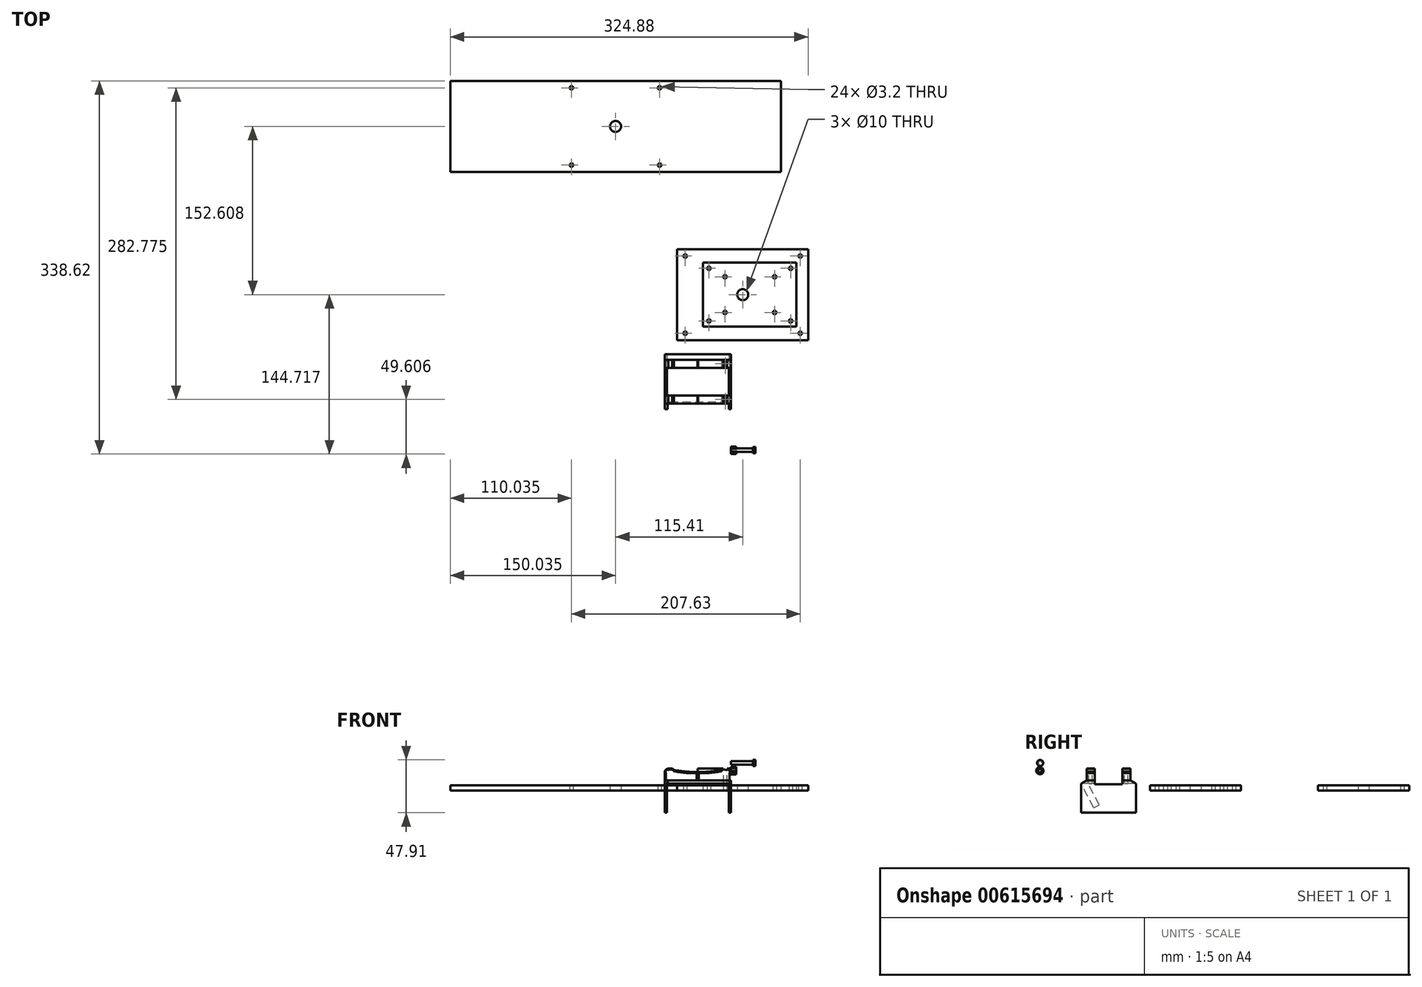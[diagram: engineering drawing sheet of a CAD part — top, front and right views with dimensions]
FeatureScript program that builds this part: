
annotation { "Feature Type Name" : "Feature", "Feature Type Description" : "" }
export const myFeature = defineFeature(function(context is Context, id is Id, definition is map)
    precondition{}
    {
        {
            var Q0;
            Q0=qCreatedBy(makeId("Right.planeOp"),FACE);
            var sketch = newSketch(context, id + "F0", { "sketchPlane" : qUnion([Q0])});
            skLineSegment(sketch, "E0.bottom", {"start": v(-19.87, 20) * mm, "end": v(-12.5, 20) * mm});
            skLineSegment(sketch, "E0.top", {"start": v(-25, -20) * mm, "end": v(25, -20) * mm});
            skLineSegment(sketch, "E0.left", {"start": v(-25, 6.62) * mm, "end": v(-25, -20) * mm});
            skLineSegment(sketch, "E0.right", {"start": v(25, 6.62) * mm, "end": v(25, -20) * mm});
            skPoint(sketch, "E0.middle", {"position": v(0, 0) * mm});
            skLineSegment(sketch, "E1", {"start": v(-12.5, 20) * mm, "end": v(-12.5, 5.9) * mm});
            skLineSegment(sketch, "E2", {"start": v(-12.5, 5.9) * mm, "end": v(0, 5.9) * mm});
            skLineSegment(sketch, "E3", {"start": v(-19.87, 20) * mm, "end": v(-19.87, 9.27) * mm});
            skLineSegment(sketch, "E4", {"start": v(-19.87, 9.27) * mm, "end": v(-25, 6.62) * mm});
            skPoint(sketch, "E5.orphan", {"position": v(-25, 20) * mm});
            skLineSegment(sketch, "E6.MirrorCS", {"start": v(12.5, 20) * mm, "end": v(12.5, 5.9) * mm});
            skLineSegment(sketch, "E7.MirrorCS", {"start": v(12.5, 5.9) * mm, "end": v(0, 5.9) * mm});
            skLineSegment(sketch, "E8.MirrorCS", {"start": v(19.87, 20) * mm, "end": v(19.87, 9.27) * mm});
            skLineSegment(sketch, "E9.MirrorCS", {"start": v(19.87, 9.27) * mm, "end": v(25, 6.62) * mm});
            skLineSegment(sketch, "E10.trimOffspring", {"start": v(12.5, 20) * mm, "end": v(19.87, 20) * mm});
            skPoint(sketch, "E11.orphan", {"position": v(25, 20) * mm});
            skCircle(sketch, "E12", {"center": v(-62.07, 25.12) * mm, "radius": 1.6 * mm});
            skCircle(sketch, "E13", {"center": v(-62.32, 18.1) * mm, "radius": 1.6 * mm});
            skCircle(sketch, "E14.cCircle", {"center": v(-62.32, 18.1) * mm, "radius": 3.2 * mm, "construction": true});
            skLineSegment(sketch, "E14.0", {"start": v(-65.79, 17.93) * mm, "end": v(-64.89, 20.43) * mm});
            skLineSegment(sketch, "E14.1", {"start": v(-64.89, 20.43) * mm, "end": v(-62.48, 21.56) * mm});
            skLineSegment(sketch, "E14.2", {"start": v(-62.48, 21.56) * mm, "end": v(-59.98, 20.66) * mm});
            skLineSegment(sketch, "E14.3", {"start": v(-59.98, 20.66) * mm, "end": v(-58.85, 18.26) * mm});
            skLineSegment(sketch, "E14.4", {"start": v(-58.85, 18.26) * mm, "end": v(-59.75, 15.75) * mm});
            skLineSegment(sketch, "E14.5", {"start": v(-59.75, 15.75) * mm, "end": v(-62.15, 14.62) * mm});
            skLineSegment(sketch, "E14.6", {"start": v(-62.15, 14.62) * mm, "end": v(-64.65, 15.52) * mm});
            skLineSegment(sketch, "E14.7", {"start": v(-64.65, 15.52) * mm, "end": v(-65.79, 17.93) * mm});
            skPoint(sketch, "E14.0.midPoint", {"position": v(-65.34, 19.18) * mm});
            skLineSegment(sketch, "E15.MirrorCS", {"start": v(-62.48, -21.56) * mm, "end": v(-59.98, -20.66) * mm});
            skLineSegment(sketch, "E16.MirrorCS", {"start": v(-64.89, -20.43) * mm, "end": v(-62.48, -21.56) * mm});
            skLineSegment(sketch, "E17.MirrorCS", {"start": v(-64.65, -15.52) * mm, "end": v(-65.79, -17.93) * mm});
            skLineSegment(sketch, "E18.MirrorCS", {"start": v(-58.85, -18.26) * mm, "end": v(-59.75, -15.75) * mm});
            skLineSegment(sketch, "E19.MirrorCS", {"start": v(-65.79, -17.93) * mm, "end": v(-64.89, -20.43) * mm});
            skLineSegment(sketch, "E20.MirrorCS", {"start": v(-62.15, -14.62) * mm, "end": v(-64.65, -15.52) * mm});
            skLineSegment(sketch, "E21.MirrorCS", {"start": v(-59.75, -15.75) * mm, "end": v(-62.15, -14.62) * mm});
            skCircle(sketch, "E22.MirrorC", {"center": v(-62.32, -18.1) * mm, "radius": 1.6 * mm});
            skLineSegment(sketch, "E23.MirrorCS", {"start": v(-59.98, -20.66) * mm, "end": v(-58.85, -18.26) * mm});
            skCircle(sketch, "E24.MirrorC", {"center": v(-62.32, -18.1) * mm, "radius": 3.2 * mm, "construction": true});
            skPoint(sketch, "E25.MirrorP", {"position": v(-65.34, -19.18) * mm});
            skSolve(sketch);
        }
        {
            var Q0;
            Q0=makeQuery(id+"F0.imprint","IMPRINT",FACE,{"disambiguationData":[TD([[makeQuery(id+"F0.imprint","IMPRINT",EDGE,{"derivedFrom":sQuery(id+"F0.wireOp",EDGE,"E0.bottom")}),-1.0]])]});
            extrude(context, id + "F1", {"entities" : qUnion([Q0]), "oppositeDirection" : true, "depth" : 60 * mm, "offsetDistance" : 25 * mm});
        }
        {
            var Q0;
            Q0=makeQuery(id+"F1.opExtrude","SWEPT_FACE",FACE,{"disambiguationData":[OSD([sQuery(id+"F0.wireOp",EDGE,"E3")])]});
            var sketch = newSketch(context, id + "F2", { "sketchPlane" : qUnion([Q0])});
            skArc(sketch, "E26", {"start": v(-56.45, 20) * mm, "mid": v(-59.1, 18.91) * mm, "end": v(-60, 16.18) * mm});
            skLineSegment(sketch, "E27", {"start": v(-30, 20) * mm, "end": v(-30, 9.27) * mm});
            skArc(sketch, "E28.MirrorCS", {"start": v(-3.55, 20) * mm, "mid": v(-0.9, 18.91) * mm, "end": v(0, 16.18) * mm});
            skArc(sketch, "E29", {"start": v(-51.52, 18.72) * mm, "mid": v(-52.28, 19.52) * mm, "end": v(-53.28, 20) * mm});
            skArc(sketch, "E30.MirrorCS", {"start": v(-8.48, 18.72) * mm, "mid": v(-7.72, 19.52) * mm, "end": v(-6.72, 20) * mm});
            skArc(sketch, "E31", {"start": v(-51.52, 18.72) * mm, "mid": v(-30, 16.9) * mm, "end": v(-8.48, 18.72) * mm});
            skPoint(sketch, "E32.orphan", {"position": v(-51.06, 16.58) * mm});
            skPoint(sketch, "E33.orphan", {"position": v(-8.94, 16.58) * mm});
            skLineSegment(sketch, "E34", {"start": v(-58.92, 9.27) * mm, "end": v(-58.92, 15.97) * mm});
            skLineSegment(sketch, "E35", {"start": v(-30.9, 15.88) * mm, "end": v(-30.9, 9.27) * mm});
            skArc(sketch, "E36", {"start": v(-51.92, 17.72) * mm, "mid": v(-41.46, 16.24) * mm, "end": v(-30.9, 15.88) * mm});
            skArc(sketch, "E37", {"start": v(-56.43, 18.92) * mm, "mid": v(-58.7, 18.3) * mm, "end": v(-58.92, 15.97) * mm});
            skArc(sketch, "E38", {"start": v(-51.92, 17.72) * mm, "mid": v(-52.22, 18.8) * mm, "end": v(-53.3, 19.1) * mm});
            skLineSegment(sketch, "E39", {"start": v(-56.43, 18.92) * mm, "end": v(-53.3, 19.1) * mm});
            skArc(sketch, "E40.MirrorCS", {"start": v(-8.08, 17.72) * mm, "mid": v(-18.54, 16.24) * mm, "end": v(-29.1, 15.88) * mm});
            skArc(sketch, "E41.MirrorCS", {"start": v(-8.08, 17.72) * mm, "mid": v(-7.78, 18.8) * mm, "end": v(-6.7, 19.1) * mm});
            skLineSegment(sketch, "E42.MirrorCS", {"start": v(-3.57, 18.92) * mm, "end": v(-6.7, 19.1) * mm});
            skArc(sketch, "E43.MirrorCS", {"start": v(-3.57, 18.92) * mm, "mid": v(-1.3, 18.3) * mm, "end": v(-1.08, 15.97) * mm});
            skLineSegment(sketch, "E44.MirrorCS", {"start": v(-1.08, 9.27) * mm, "end": v(-1.08, 15.97) * mm});
            skLineSegment(sketch, "E45.MirrorCS", {"start": v(-29.1, 15.88) * mm, "end": v(-29.1, 9.27) * mm});
            skSolve(sketch);
        }
        {
            var Q0;
            {var subQ0=sQuery(id+"F2.wireOp",EDGE,"E26");var subQ1=sQuery(id+"F0.wireOp",EDGE,"E3");var subQ4=makeQuery(id+"F1.opExtrude","CAP_EDGE",EDGE,{"disambiguationData":[OSD([subQ1])],"isStart":false});var subQ5=makeQuery(id+"F2.imprint","INTERSECT",VERTEX,{"disambiguationData":[OD(1.0)],"derivedFrom":[subQ4,subQ0]});Q0=makeQuery(id+"F2.imprint","IMPRINT",FACE,{"disambiguationData":[TD([[makeQuery(id+"F2.imprint","IMPRINT",EDGE,{"disambiguationData":[TD([[subQ5,1.0]])],"derivedFrom":subQ0}),-1.0]])]});}
            var Q1;
            {var subQ0=sQuery(id+"F2.wireOp",EDGE,"E28.MirrorCS");var subQ1=sQuery(id+"F0.wireOp",EDGE,"E3");var subQ4=makeQuery(id+"F1.opExtrude","CAP_EDGE",EDGE,{"disambiguationData":[OSD([subQ1])],"isStart":true});var subQ5=makeQuery(id+"F2.imprint","INTERSECT",VERTEX,{"disambiguationData":[OD(1.0)],"derivedFrom":[subQ4,subQ0]});Q1=makeQuery(id+"F2.imprint","IMPRINT",FACE,{"disambiguationData":[TD([[makeQuery(id+"F2.imprint","IMPRINT",EDGE,{"disambiguationData":[TD([[subQ5,1.0]])],"derivedFrom":subQ0}),1.0]])]});}
            var Q2;
            {var subQ5=sQuery(id+"F2.wireOp",EDGE,"E29");Q2=makeQuery(id+"F2.imprint","IMPRINT",FACE,{"disambiguationData":[TD([[makeQuery(id+"F2.imprint","IMPRINT",EDGE,{"derivedFrom":subQ5}),-1.0]])]});}
            var Q3;
            {var subQ5=sQuery(id+"F2.wireOp",EDGE,"E30.MirrorCS");Q3=makeQuery(id+"F2.imprint","IMPRINT",FACE,{"disambiguationData":[TD([[makeQuery(id+"F2.imprint","IMPRINT",EDGE,{"derivedFrom":subQ5}),1.0]])]});}
            var Q4;
            {var subQ0=sQuery(id+"F2.wireOp",EDGE,"E34");Q4=makeQuery(id+"F2.imprint","IMPRINT",FACE,{"disambiguationData":[TD([[makeQuery(id+"F2.imprint","IMPRINT",EDGE,{"derivedFrom":subQ0}),-1.0]])]});}
            var Q5;
            Q5=makeQuery(id+"F2.imprint","IMPRINT",FACE,{"disambiguationData":[TD([[makeQuery(id+"F2.imprint","IMPRINT",EDGE,{"derivedFrom":sQuery(id+"F2.wireOp",EDGE,"E40.MirrorCS")}),1.0]])]});
            var Q6;
            Q6=makeQuery(id+"F1.opExtrude","SWEPT_BODY",BODY,{"disambiguationData":[OSD([sQuery(id+"F0.wireOp",EDGE,"E0.bottom"),sQuery(id+"F0.wireOp",EDGE,"E0.top"),sQuery(id+"F0.wireOp",EDGE,"E0.left"),sQuery(id+"F0.wireOp",EDGE,"E0.right"),sQuery(id+"F0.wireOp",EDGE,"E1"),sQuery(id+"F0.wireOp",EDGE,"E2"),sQuery(id+"F0.wireOp",EDGE,"E3"),sQuery(id+"F0.wireOp",EDGE,"E4"),sQuery(id+"F0.wireOp",EDGE,"E6.MirrorCS"),sQuery(id+"F0.wireOp",EDGE,"E7.MirrorCS"),sQuery(id+"F0.wireOp",EDGE,"E8.MirrorCS"),sQuery(id+"F0.wireOp",EDGE,"E9.MirrorCS"),sQuery(id+"F0.wireOp",EDGE,"E10.trimOffspring")])]});
            extrude(context, id + "F3", {"entities" : qUnion([Q0, Q1, Q2, Q3, Q4, Q5]), "operationType" : NewBodyOperationType.REMOVE, "endBound" : BoundingType.THROUGH_ALL, "oppositeDirection" : true, "depth" : 25 * mm, "endBoundEntityBody" : qUnion([Q6]), "offsetDistance" : 25 * mm});
        }
        {
            var Q0;
            Q0=makeQuery(id+"F1.opExtrude","SWEPT_FACE",FACE,{"disambiguationData":[OSD([sQuery(id+"F0.wireOp",EDGE,"E0.left")])]});
            var sketch = newSketch(context, id + "F4", { "sketchPlane" : qUnion([Q0])});
            skLineSegment(sketch, "E46.top", {"start": v(-57.93, -20) * mm, "end": v(-1.88, -20) * mm});
            skLineSegment(sketch, "E46.left", {"start": v(-57.93, 5.02) * mm, "end": v(-57.93, -20) * mm});
            skLineSegment(sketch, "E46.right", {"start": v(-1.88, 5.02) * mm, "end": v(-1.88, -20) * mm});
            skLineSegment(sketch, "E47", {"start": v(-57.93, 5.02) * mm, "end": v(-57.93, 6.62) * mm});
            skLineSegment(sketch, "E48", {"start": v(-1.88, 5.02) * mm, "end": v(-1.88, 6.62) * mm});
            skSolve(sketch);
        }
        {
            var Q0;
            Q0=makeQuery(id+"F4.imprint","IMPRINT",FACE,{"disambiguationData":[TD([[makeQuery(id+"F4.imprint","IMPRINT",EDGE,{"derivedFrom":sQuery(id+"F4.wireOp",EDGE,"E46.bottom")}),-1.0]])]});
            var Q1;
            Q1=makeQuery(id+"F4.imprint","IMPRINT",FACE,{"disambiguationData":[TD([[makeQuery(id+"F4.imprint","IMPRINT",EDGE,{"derivedFrom":sQuery(id+"F4.wireOp",EDGE,"E46.top")}),1.0]])]});
            extrude(context, id + "F5", {"entities" : qUnion([Q0, Q1]), "operationType" : NewBodyOperationType.REMOVE, "endBound" : BoundingType.THROUGH_ALL, "oppositeDirection" : true, "depth" : 25 * mm, "offsetDistance" : 25 * mm});
        }
        {
            var Q0;
            Q0=makeQuery(id+"F1.opExtrude","SWEPT_FACE",FACE,{"disambiguationData":[OSD([sQuery(id+"F0.wireOp",EDGE,"E4")])]});
            var sketch = newSketch(context, id + "F6", { "sketchPlane" : qUnion([Q0])});
            skLineSegment(sketch, "E49", {"start": v(-57.48, -19.18) * mm, "end": v(-57.48, -13.4) * mm});
            skLineSegment(sketch, "E50", {"start": v(-57.48, -13.4) * mm, "end": v(-1.08, -13.4) * mm});
            skLineSegment(sketch, "E51", {"start": v(-1.08, -13.4) * mm, "end": v(-1.08, -19.18) * mm});
            skSolve(sketch);
        }
        {
            var Q0;
            {var subQ9=sQuery(id+"F6.wireOp",EDGE,"E49");Q0=makeQuery(id+"F6.imprint","IMPRINT",FACE,{"disambiguationData":[TD([[makeQuery(id+"F6.imprint","IMPRINT",EDGE,{"derivedFrom":subQ9}),-1.0]])]});}
            extrude(context, id + "F7", {"entities" : qUnion([Q0]), "operationType" : NewBodyOperationType.REMOVE, "oppositeDirection" : true, "depth" : 25 * mm, "offsetDistance" : 25 * mm});
        }
        {
            var Q0;
            Q0=makeQuery(id+"F0.imprint","IMPRINT",FACE,{"disambiguationData":[TD([[makeQuery(id+"F0.imprint","IMPRINT",EDGE,{"derivedFrom":sQuery(id+"F0.wireOp",EDGE,"E12")}),1.0]])]});
            extrude(context, id + "F8", {"entities" : qUnion([Q0]), "depth" : 20 * mm, "offsetDistance" : 25 * mm});
        }
        {
            var Q0;
            Q0=makeQuery(id+"F8.opExtrude","CAP_FACE",FACE,{"disambiguationData":[OSD([sQuery(id+"F0.wireOp",EDGE,"E12")])],"isStart":false});
            var sketch = newSketch(context, id + "F9", { "sketchPlane" : qUnion([Q0])});
            skCircle(sketch, "E52", {"center": v(-62.07, 25.12) * mm, "radius": 2.79 * mm});
            skSolve(sketch);
        }
        {
            var Q0;
            Q0=makeQuery(id+"F9.imprint","IMPRINT",FACE,{"disambiguationData":[TD([[makeQuery(id+"F9.imprint","IMPRINT",EDGE,{"derivedFrom":sQuery(id+"F9.wireOp",EDGE,"E52")}),1.0]])]});
            var Q1;
            Q1=makeQuery(id+"F9.imprint","IMPRINT",FACE,{"disambiguationData":[TD([[makeQuery(id+"F9.imprint","IMPRINT",EDGE,{"derivedFrom":makeQuery(id+"F8.opExtrude","CAP_EDGE",EDGE,{"disambiguationData":[OSD([sQuery(id+"F0.wireOp",EDGE,"E12")])],"isStart":false})}),1.0]])]});
            extrude(context, id + "F10", {"entities" : qUnion([Q0, Q1]), "operationType" : NewBodyOperationType.ADD, "depth" : 2.5 * mm, "offsetDistance" : 25 * mm});
        }
        {
            var Q0;
            Q0=makeQuery(id+"F0.imprint","IMPRINT",FACE,{"disambiguationData":[TD([[makeQuery(id+"F0.imprint","IMPRINT",EDGE,{"derivedFrom":sQuery(id+"F0.wireOp",EDGE,"E13")}),-1.0]])]});
            extrude(context, id + "F11", {"entities" : qUnion([Q0]), "depth" : 5 * mm, "offsetDistance" : 25 * mm});
        }
        {
            var Q0;
            Q0=makeQuery(id+"F3.boolean.opBoolean","SPLIT",FACE,{"disambiguationData":[TD([makeQuery(id+"F3.opExtrude","SWEPT_FACE",FACE,{"disambiguationData":[OSD([sQuery(id+"F2.wireOp",EDGE,"E28.MirrorCS")])]})])],"derivedFrom":makeQuery(id+"F1.opExtrude","SWEPT_FACE",FACE,{"disambiguationData":[OSD([sQuery(id+"F0.wireOp",EDGE,"E0.bottom")])]})});
            var sketch = newSketch(context, id + "F12", { "sketchPlane" : qUnion([Q0])});
            skCircle(sketch, "E53", {"center": v(-4.98, -16.18) * mm, "radius": 1.6 * mm});
            skPoint(sketch, "E53.centerSnap0", {"position": v(-3.24, -16.18) * mm});
            skPoint(sketch, "E53.centerSnap1", {"position": v(-4.98, -19.87) * mm});
            skSolve(sketch);
        }
        {
            var Q0;
            Q0=makeQuery(id+"F12.imprint","IMPRINT",FACE,{"disambiguationData":[TD([[makeQuery(id+"F12.imprint","IMPRINT",EDGE,{"derivedFrom":sQuery(id+"F12.wireOp",EDGE,"E53")}),1.0]])]});
            extrude(context, id + "F13", {"entities" : qUnion([Q0]), "operationType" : NewBodyOperationType.REMOVE, "oppositeDirection" : true, "depth" : 25 * mm, "offsetDistance" : 25 * mm});
        }
        {
            var Q0;
            Q0=qCreatedBy(makeId("Top.planeOp"),FACE);
            var sketch = newSketch(context, id + "F14", { "sketchPlane" : qUnion([Q0])});
            skLineSegment(sketch, "E54.bottom", {"start": v(-25.12, 49.88) * mm, "end": v(59.63, 49.88) * mm});
            skLineSegment(sketch, "E54.top", {"start": v(-25.12, 107.97) * mm, "end": v(59.63, 107.97) * mm});
            skLineSegment(sketch, "E54.left", {"start": v(-25.12, 49.88) * mm, "end": v(-25.12, 107.97) * mm});
            skLineSegment(sketch, "E54.right", {"start": v(59.63, 49.88) * mm, "end": v(59.63, 107.97) * mm});
            skLineSegment(sketch, "E55", {"start": v(-25.12, 78.93) * mm, "end": v(59.63, 78.93) * mm, "construction": true});
            skCircle(sketch, "E56", {"center": v(39.75, 62.74) * mm, "radius": 1.6 * mm});
            skCircle(sketch, "E57.MirrorC", {"center": v(39.75, 95.11) * mm, "radius": 1.6 * mm});
            skLineSegment(sketch, "E58.bottom", {"start": v(70.25, 37.63) * mm, "end": v(-48.62, 37.63) * mm});
            skLineSegment(sketch, "E58.top", {"start": v(70.25, 120.23) * mm, "end": v(-48.62, 120.23) * mm});
            skLineSegment(sketch, "E58.left", {"start": v(70.25, 37.63) * mm, "end": v(70.25, 120.23) * mm});
            skLineSegment(sketch, "E58.right", {"start": v(-48.62, 37.63) * mm, "end": v(-48.62, 120.23) * mm});
            skPoint(sketch, "E58.middle", {"position": v(10.82, 78.93) * mm});
            skCircle(sketch, "E59", {"center": v(63.04, 43.87) * mm, "radius": 1.6 * mm});
            skCircle(sketch, "E60.MirrorC", {"center": v(63.04, 113.98) * mm, "radius": 1.6 * mm});
            skCircle(sketch, "E61.MirrorC", {"center": v(-41.4, 43.87) * mm, "radius": 1.6 * mm});
            skCircle(sketch, "E62.MirrorC", {"center": v(-41.4, 113.98) * mm, "radius": 1.6 * mm});
            skCircle(sketch, "E63", {"center": v(54.37, 55.05) * mm, "radius": 1.6 * mm});
            skCircle(sketch, "E64.MirrorC", {"center": v(54.37, 102.8) * mm, "radius": 1.6 * mm});
            skLineSegment(sketch, "E65", {"start": v(17.25, 107.97) * mm, "end": v(17.25, 49.88) * mm, "construction": true});
            skCircle(sketch, "E66.MirrorC", {"center": v(-19.86, 55.05) * mm, "radius": 1.6 * mm});
            skCircle(sketch, "E67.MirrorC", {"center": v(-19.86, 102.8) * mm, "radius": 1.6 * mm});
            skCircle(sketch, "E68.MirrorC", {"center": v(-5.25, 95.11) * mm, "radius": 1.6 * mm});
            skCircle(sketch, "E69.MirrorC", {"center": v(-5.25, 62.74) * mm, "radius": 1.6 * mm});
            skLineSegment(sketch, "E70.bottom", {"start": v(45.44, 272.83) * mm, "end": v(-254.63, 272.83) * mm});
            skLineSegment(sketch, "E70.top", {"start": v(45.44, 190.23) * mm, "end": v(-254.63, 190.23) * mm});
            skLineSegment(sketch, "E70.left", {"start": v(45.44, 272.83) * mm, "end": v(45.44, 190.23) * mm});
            skLineSegment(sketch, "E70.right", {"start": v(-254.63, 272.83) * mm, "end": v(-254.63, 190.23) * mm});
            skPoint(sketch, "E70.middle", {"position": v(-104.6, 231.53) * mm});
            skLineSegment(sketch, "E71", {"start": v(-254.63, 231.53) * mm, "end": v(45.44, 231.53) * mm, "construction": true});
            skLineSegment(sketch, "E72", {"start": v(-104.6, 190.23) * mm, "end": v(-104.6, 272.83) * mm});
            skCircle(sketch, "E73", {"center": v(-144.6, 196.48) * mm, "radius": 1.6 * mm});
            skCircle(sketch, "E74.MirrorC", {"center": v(-144.6, 266.6) * mm, "radius": 1.6 * mm});
            skCircle(sketch, "E75.MirrorC", {"center": v(-64.6, 196.48) * mm, "radius": 1.6 * mm});
            skCircle(sketch, "E76.MirrorC", {"center": v(-64.6, 266.6) * mm, "radius": 1.6 * mm});
            skCircle(sketch, "E77", {"center": v(-104.6, 231.53) * mm, "radius": 5 * mm});
            skSolve(sketch);
        }
        {
            var Q0;
            Q0=makeQuery(id+"F3.boolean.opBoolean","SPLIT",FACE,{"disambiguationData":[TD([makeQuery(id+"F3.opExtrude","SWEPT_FACE",FACE,{"disambiguationData":[OSD([sQuery(id+"F2.wireOp",EDGE,"E28.MirrorCS")])]})])],"derivedFrom":makeQuery(id+"F1.opExtrude","SWEPT_FACE",FACE,{"disambiguationData":[OSD([sQuery(id+"F0.wireOp",EDGE,"E10.trimOffspring")])]})});
            var sketch = newSketch(context, id + "F15", { "sketchPlane" : qUnion([Q0])});
            skCircle(sketch, "E78", {"center": v(-4.98, 16.18) * mm, "radius": 1.6 * mm});
            skPoint(sketch, "E78.centerSnap0", {"position": v(-4.98, 19.87) * mm});
            skPoint(sketch, "E78.centerSnap1", {"position": v(-6.72, 16.18) * mm});
            skCircle(sketch, "E79", {"center": v(40.74, 61.93) * mm, "radius": 1.6 * mm});
            skCircle(sketch, "E80.MirrorC", {"center": v(40.74, 95.93) * mm, "radius": 1.6 * mm});
            skSolve(sketch);
        }
        {
            var Q0;
            Q0=makeQuery(id+"F15.imprint","IMPRINT",FACE,{"disambiguationData":[TD([[makeQuery(id+"F15.imprint","IMPRINT",EDGE,{"derivedFrom":sQuery(id+"F15.wireOp",EDGE,"E78")}),1.0]])]});
            extrude(context, id + "F16", {"entities" : qUnion([Q0]), "operationType" : NewBodyOperationType.REMOVE, "oppositeDirection" : true, "depth" : 25 * mm, "offsetDistance" : 25 * mm});
        }
        {
            var Q0;
            Q0=makeQuery(id+"F14.imprint","IMPRINT",FACE,{"disambiguationData":[TD([[makeQuery(id+"F14.imprint","IMPRINT",EDGE,{"derivedFrom":sQuery(id+"F14.wireOp",EDGE,"E54.bottom")}),1.0]])]});
            extrude(context, id + "F17", {"entities" : qUnion([Q0]), "depth" : 5 * mm, "offsetDistance" : 25 * mm});
        }
        {
            var Q0;
            Q0=makeQuery(id+"F14.imprint","IMPRINT",FACE,{"disambiguationData":[TD([[makeQuery(id+"F14.imprint","IMPRINT",EDGE,{"derivedFrom":sQuery(id+"F14.wireOp",EDGE,"E54.bottom")}),-1.0]])]});
            var Q1;
            Q1=makeQuery(id+"F14.imprint","IMPRINT",FACE,{"disambiguationData":[TD([[makeQuery(id+"F14.imprint","IMPRINT",EDGE,{"derivedFrom":sQuery(id+"F14.wireOp",EDGE,"E54.bottom")}),1.0]])]});
            var Q2;
            Q2=makeQuery(id+"F14.imprint","IMPRINT",FACE,{"disambiguationData":[TD([[makeQuery(id+"F14.imprint","IMPRINT",EDGE,{"derivedFrom":sQuery(id+"F14.wireOp",EDGE,"E69.MirrorC")}),-1.0]])]});
            var Q3;
            Q3=makeQuery(id+"F14.imprint","IMPRINT",FACE,{"disambiguationData":[TD([[makeQuery(id+"F14.imprint","IMPRINT",EDGE,{"derivedFrom":sQuery(id+"F14.wireOp",EDGE,"E68.MirrorC")}),1.0]])]});
            var Q4;
            Q4=makeQuery(id+"F14.imprint","IMPRINT",FACE,{"disambiguationData":[TD([[makeQuery(id+"F14.imprint","IMPRINT",EDGE,{"derivedFrom":sQuery(id+"F14.wireOp",EDGE,"E57.MirrorC")}),-1.0]])]});
            var Q5;
            Q5=makeQuery(id+"F14.imprint","IMPRINT",FACE,{"disambiguationData":[TD([[makeQuery(id+"F14.imprint","IMPRINT",EDGE,{"derivedFrom":sQuery(id+"F14.wireOp",EDGE,"E56")}),1.0]])]});
            extrude(context, id + "F18", {"entities" : qUnion([Q0, Q1, Q2, Q3, Q4, Q5]), "depth" : 5 * mm, "offsetDistance" : 25 * mm});
        }
        {
            var Q0;
            Q0=makeQuery(id+"F18.opExtrude","CAP_FACE",FACE,{"disambiguationData":[OSD([sQuery(id+"F14.wireOp",EDGE,"E56"),sQuery(id+"F14.wireOp",EDGE,"E57.MirrorC"),sQuery(id+"F14.wireOp",EDGE,"E58.bottom"),sQuery(id+"F14.wireOp",EDGE,"E58.top"),sQuery(id+"F14.wireOp",EDGE,"E58.left"),sQuery(id+"F14.wireOp",EDGE,"E58.right")])],"isStart":true});
            var sketch = newSketch(context, id + "F19", { "sketchPlane" : qUnion([Q0])});
            skCircle(sketch, "E81", {"center": v(10.82, -78.93) * mm, "radius": 5 * mm});
            skPoint(sketch, "E81.centerSnap0", {"position": v(10.82, -37.63) * mm});
            skPoint(sketch, "E81.centerSnap1", {"position": v(70.25, -78.93) * mm});
            skSolve(sketch);
        }
        {
            var Q0;
            Q0=makeQuery(id+"F19.imprint","IMPRINT",FACE,{"disambiguationData":[TD([[makeQuery(id+"F19.imprint","IMPRINT",EDGE,{"derivedFrom":sQuery(id+"F19.wireOp",EDGE,"E81")}),1.0]])]});
            extrude(context, id + "F20", {"entities" : qUnion([Q0]), "operationType" : NewBodyOperationType.REMOVE, "oppositeDirection" : true, "depth" : 25 * mm, "offsetDistance" : 25 * mm});
        }
        {
            var Q0;
            {var subQ0=sQuery(id+"F14.wireOp",EDGE,"E70.right");Q0=makeQuery(id+"F14.imprint","IMPRINT",FACE,{"disambiguationData":[TD([[makeQuery(id+"F14.imprint","IMPRINT",EDGE,{"derivedFrom":subQ0}),1.0]])]});}
            var Q1;
            {var subQ1=sQuery(id+"F14.wireOp",EDGE,"E70.left");Q1=makeQuery(id+"F14.imprint","IMPRINT",FACE,{"disambiguationData":[TD([[makeQuery(id+"F14.imprint","IMPRINT",EDGE,{"derivedFrom":subQ1}),-1.0]])]});}
            extrude(context, id + "F21", {"entities" : qUnion([Q0, Q1]), "depth" : 5 * mm, "offsetDistance" : 25 * mm});
        }
    });
